# Revit family: IS_SensorflowNew_A7564_BIM_NL
name_source: partatom
category: Plumbing Fixtures
revit_build: Autodesk Revit 2017 (Build: 20160225_1515(x64)
units: mm (PartAtom-declared; Revit-internal decimal feet)

## family parameters
Always vertical = No
Cut with Voids When Loaded = No
OmniClass Number = 23.45.55.14
OmniClass Title = Single Faucets
Part Type = Normal
Room Calculation Point = No
Round Connector Dimension = Use Diameter
Shared = No
Work Plane-Based = No

## types (1)
- A7564AA - SENSORFLOW NEW BSN EL EXP PA MIX MNS
    Accesoires = https://www.idealstandard.nl
    Afmetingen = 67 x 221 x 72 mm
    Afwerking = Chrom
    Artikelnummer = A7564AA
    Artikelomschrijving = Sensorflow Basin mixer electronic exposed panel mounted with temperature mix with mains power
    Artikelreferentie = SENSORFLOW BSN EL EXP PA MIX BTR
    Auteur = Ideal Standard
    BIMObjectName = IS_IdealStandard_WashbasinTaps_Sensorflow_A7564
    BIMobject category = Sanitary
    BIMobject main category = Taps & Mixer
    Barcode = 4015413351157
    Bedieningkraan = Kein Tastendruck
    Bedieningkraanwerk = Sensor aktiviert
    Beschrijvinggarantie = Herstellergarantie
    BimObjectNaam = IS_IdealStandard_WashbasinTaps_Sensorflow_A7564
    Brand url = https://www.idealstandard.nl
    Breedte = 72.408802
    BrutoGewicht = 0
    CisternCapacity = 0.00 m³
    Cost = 0 $
    Date of publishing = 11/01/2021
    Description = Sensorflow Basin mixer electronic exposed panel mounted with temperature mix with mains power
    Diepte = 335 mm  [stored 1.09908 ft]
    Douchebak = No
    DrainSize = 0 mm  [stored 0 ft]
    DuurEenheid = Jaar
    Edition number = 1
    Eigenschappen = Basin mixer electronic exposed panel mounted with temperature mix with mains power
    FaucetFunction = Electronic
    FaucetOperation = No-Touch
    FaucetTopDescription = No-Touch Electronic Sensor Tap Mixer
    FaucetType = Sensorflow Mixer tap
    FlushRate = 0.00 m³
    FlushingRate = 0
    Functiekraanwerk = No-touch elektronische sensor-mengkraan
    GTIN code = https://4015413351157
    Garantieonderdelen = 5
    Garantieunits = Jaar
    GrootteAfvoergat = 0
    HasGrabHandles = No
    HasIntegralShutOffDevice = No
    HasTray = No
    Heefthandvaten = No
    Hoogte = 66.7026844024658
    Hulp = https://www.idealstandard.nl
    IFC Classification = Sanitary Terminal
    IfcExportAs = IfcValveType
    IfcExportType = FAUCET
    InletConnectionSize = 0 mm  [stored 0 ft]
    Installatieinstructies = https://www.idealstandard.nl
    Installation instructions = https://www.idealstandard.nl
    IsAutomaticFlush = No
    IsBuiltIn = No
    IsHighPressure = No
    IsSingleFlush = No
    Keynote = n /a
    Klepmechanisme = n /a
    Kleur = Chrom
    Lengte = 221 mm
    Manufacturer = Ideal Standard
    Manufacturer name = Ideal Standard
    ManufacturerURL = https://www.idealstandard.nl
    Materiaal = Messing
    Material main = Brass
    Material secondary = Chrome
    MaterialThickness = 0 mm  [stored 0 ft]
    Merk = Ideal Standard
    Model = A7564AA
    Montageinstuctie = https://www.idealstandard.nl
    NBS Reference Code = 45-35-70/371
    NBS Reference Description = Water supply fittings for wash basins and troughs
    Name = WashbasinTaps_Sensorflow_A7564_IdealStandard
    NettWeight = 1,90 KG
    Nettogewicht = 1.9
    NominalDepth = 335 mm  [stored 1.09908 ft]
    NominalHeight = 67 mm
    NominalLength = 221 mm
    NominalWidth = 72 mm
    Normen = WashbasinTaps_Sensorflow_A7564_IdealStandard
    OppervlakteEenheid = millimeter
    OutletConnectionSize = 0 mm  [stored 0 ft]
    Overloop = 0 mm  [stored 0 ft]
    Product Guid = e2bde0f0-adac-40d5-9cf8-d4e99c081c05
    Product SKU = A7564
    Product certification = https://www.idealstandard.nl
    Product data url = https://bimobject.com
    Product family = Sensorflow
    Product group = Mixer
    Product name = SENSORFLOW NEW BSN EL EXP PA MIX MNS
    Product url = https://www.idealstandard.nl
    ProductInformation = https://www.idealstandard.nl
    ProductSoort = Wasserhähne
    Productinformatie = https://www.idealstandard.nl
    QR code = http://bimobject.com
    Referentie = SENSORFLOW NEW BSN EL EXP PA MIX MNS
    Revisie = 1
    SeatHasCover = No
    Shape = Cylindrical
    Size = 67 x 221 x 72 mm
    Space = internal
    SpareParts = https://www.idealstandard.nl
    SpilloverLevel = 0 mm  [stored 0 ft]
    Technical description = https://www.idealstandard.nl
    Telefoonnummer = 077 355 08 08
    TestPressure = 10 bar
    Testdruk = 10 bar
    Typeconnectie = Sanitärinstallation
    UNSPSC Code = 301815
    URL = https://www.idealstandard.nl
    Uniclass 1.4 Code = L725111
    Uniclass 1.4 Description = Mixer taps
    Uniclass 2.0 Code = PR-35-79-95
    Uniclass 2.0 Description = Wash Basin and Trough Water Supply Fittings
    Uniclass 2015 Code = Pr_40_20_87_98
    Uniclass 2015 Name = Washbasin taps
    Uniclass2015Beschrijving = Wash Basin and Trough Water Supply Fittings
    Uniclass2015Code = Pr_40_20_87_98
    Uniclass2015Referentie = Pr_40_20_87_98
    Uniclass2015Title = Washbasin taps
    Uniclass2015Version = v1.20
    Urlproducent = https://www.idealstandard.nl
    ValutaEenheid = €
    Versie = 1
    Version = 1
    Vervangingskosten = 0
    VolumeUnits = Litres
    Volumeunits = Liter
    Vorm = Cilindrisch
    WRASURL = https://www.wrasapprovals.co.uk
    WarrantyDescription = Manufacturer Warranty
    WarrantyDurationParts = 5
    WarrantyDurationUnit = Years
    Wisselstukken = https://www.idealstandard.nl

note: [stored X ft] marks values corroborated as IEEE doubles in the binary element streams (Revit-internal decimal feet)

## geometry (parser evidence)
native form markers: Blend x2, Sweep x2
no freeform markers — native parametric forms only
